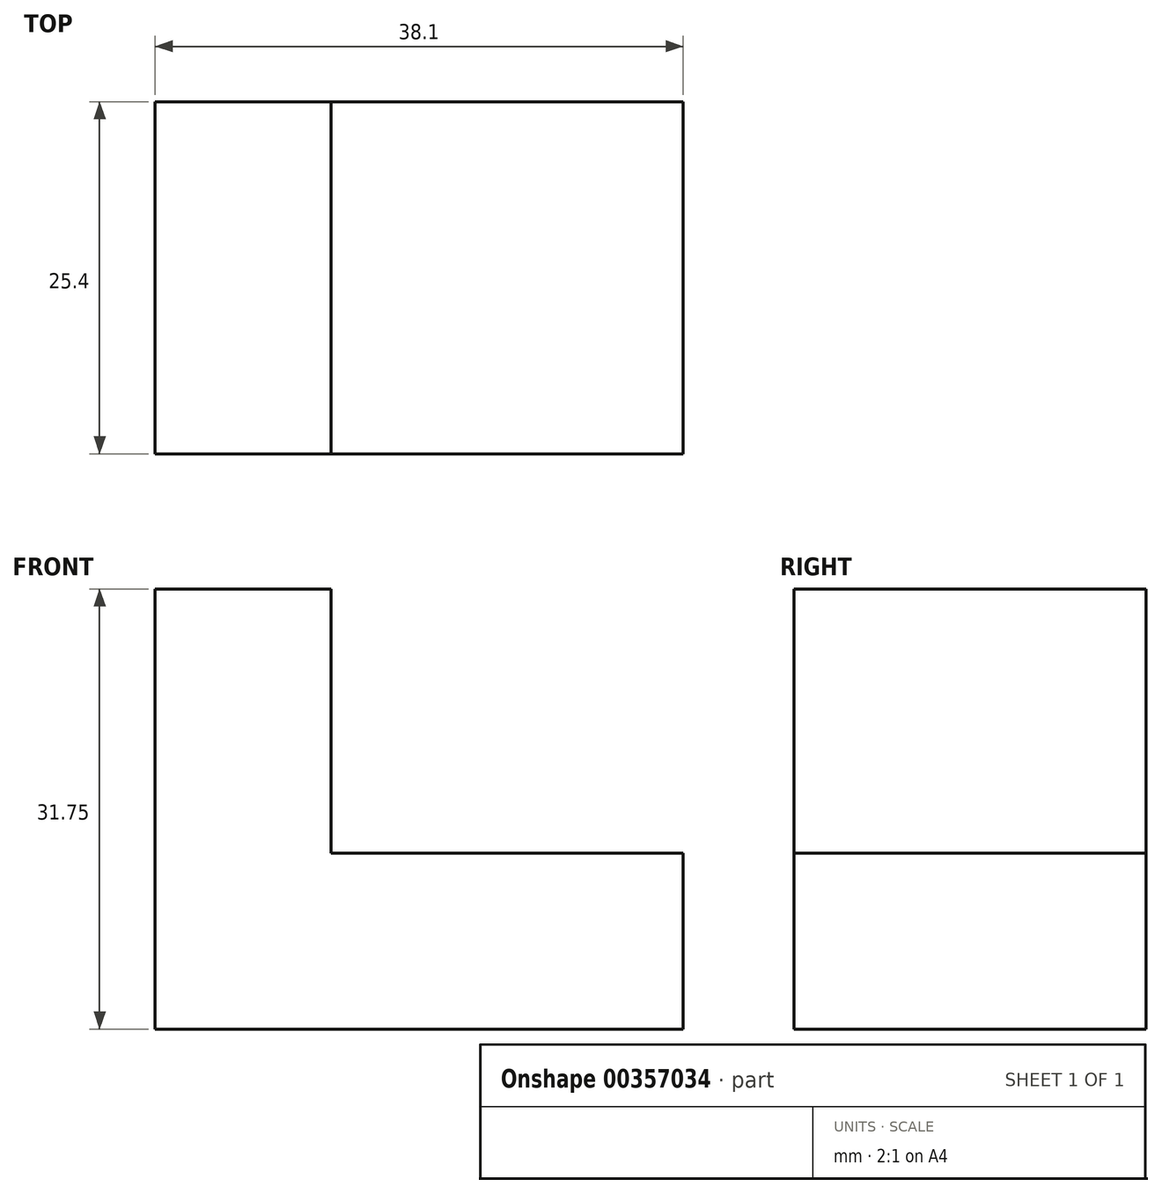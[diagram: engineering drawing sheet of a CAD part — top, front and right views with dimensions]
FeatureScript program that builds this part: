
annotation { "Feature Type Name" : "Feature", "Feature Type Description" : "" }
export const myFeature = defineFeature(function(context is Context, id is Id, definition is map)
    precondition{}
    {
        {
            var Q0;
            Q0=qCreatedBy(makeId("Front.planeOp"),FACE);
            var sketch = newSketch(context, id + "F0", { "sketchPlane" : qUnion([Q0])});
            skLineSegment(sketch, "E0", {"start": v(0, 0) * mm, "end": v(38.1, 0) * mm});
            skLineSegment(sketch, "E1", {"start": v(38.1, 0) * mm, "end": v(38.1, 12.7) * mm});
            skLineSegment(sketch, "E2", {"start": v(38.1, 12.7) * mm, "end": v(12.7, 12.7) * mm});
            skLineSegment(sketch, "E3", {"start": v(12.7, 12.7) * mm, "end": v(12.7, 31.75) * mm});
            skLineSegment(sketch, "E4", {"start": v(12.7, 31.75) * mm, "end": v(0, 31.75) * mm});
            skLineSegment(sketch, "E5", {"start": v(0, 31.75) * mm, "end": v(0, 0) * mm});
            skSolve(sketch);
        }
        {
            var Q0;
            Q0 = qSketchRegion(id + "F0", true);
            extrude(context, id + "F1", {"entities" : qUnion([Q0]), "depth" : 25.4 * mm});
        }
    });
